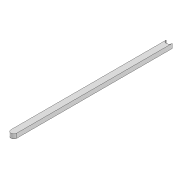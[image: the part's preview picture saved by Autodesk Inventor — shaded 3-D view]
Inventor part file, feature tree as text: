
AUTODESK INVENTOR PART (.ipt)
format: ipt  version: 2022 (Build 260153000, 153)  size: 80,896 bytes
history: native  units: mm
features: extrude x1, sketch x1
ambient origin geometry x8: Origin, YZ Plane, XZ Plane, XY Plane, X Axis, Y Axis, Z Axis, Center Point
bodies: Solid1 (feature_tree)
feature tree (2):
  extrude  "Extrusion1"  Depth=8.0mm
  sketch  "Sketch1"  dims[d0=210.0mm d1=8.0mm d2=6.0mm d3=0.0mm]
